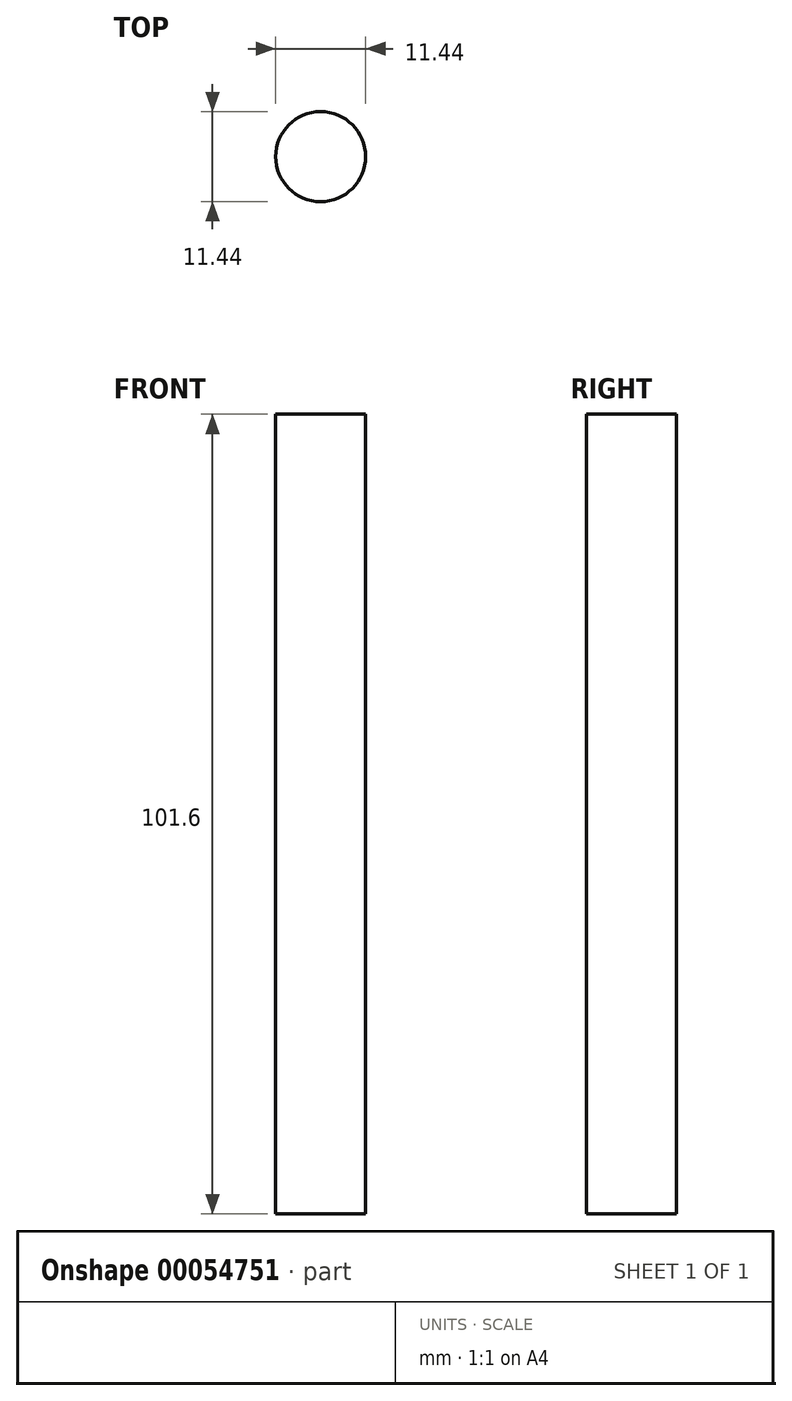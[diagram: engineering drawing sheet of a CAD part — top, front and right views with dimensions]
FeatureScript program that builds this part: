
annotation { "Feature Type Name" : "Feature", "Feature Type Description" : "" }
export const myFeature = defineFeature(function(context is Context, id is Id, definition is map)
    precondition{}
    {
        {
            var Q0;
            Q0=qCreatedBy(makeId("Top.planeOp"),FACE);
            var sketch = newSketch(context, id + "F0", { "sketchPlane" : qUnion([Q0])});
            skCircle(sketch, "E0", {"center": v(0, 0) * mm, "radius": 5.72 * mm});
            skSolve(sketch);
        }
        {
            var Q0;
            Q0=makeQuery(id+"F0.imprint","IMPRINT",FACE,{"disambiguationData":[TD([[makeQuery(id+"F0.imprint","IMPRINT",EDGE,{"derivedFrom":sQuery(id+"F0.wireOp",EDGE,"E0")}),1.0]])]});
            extrude(context, id + "F1", {"entities" : qUnion([Q0]), "depth" : 101.6 * mm});
        }
    });
